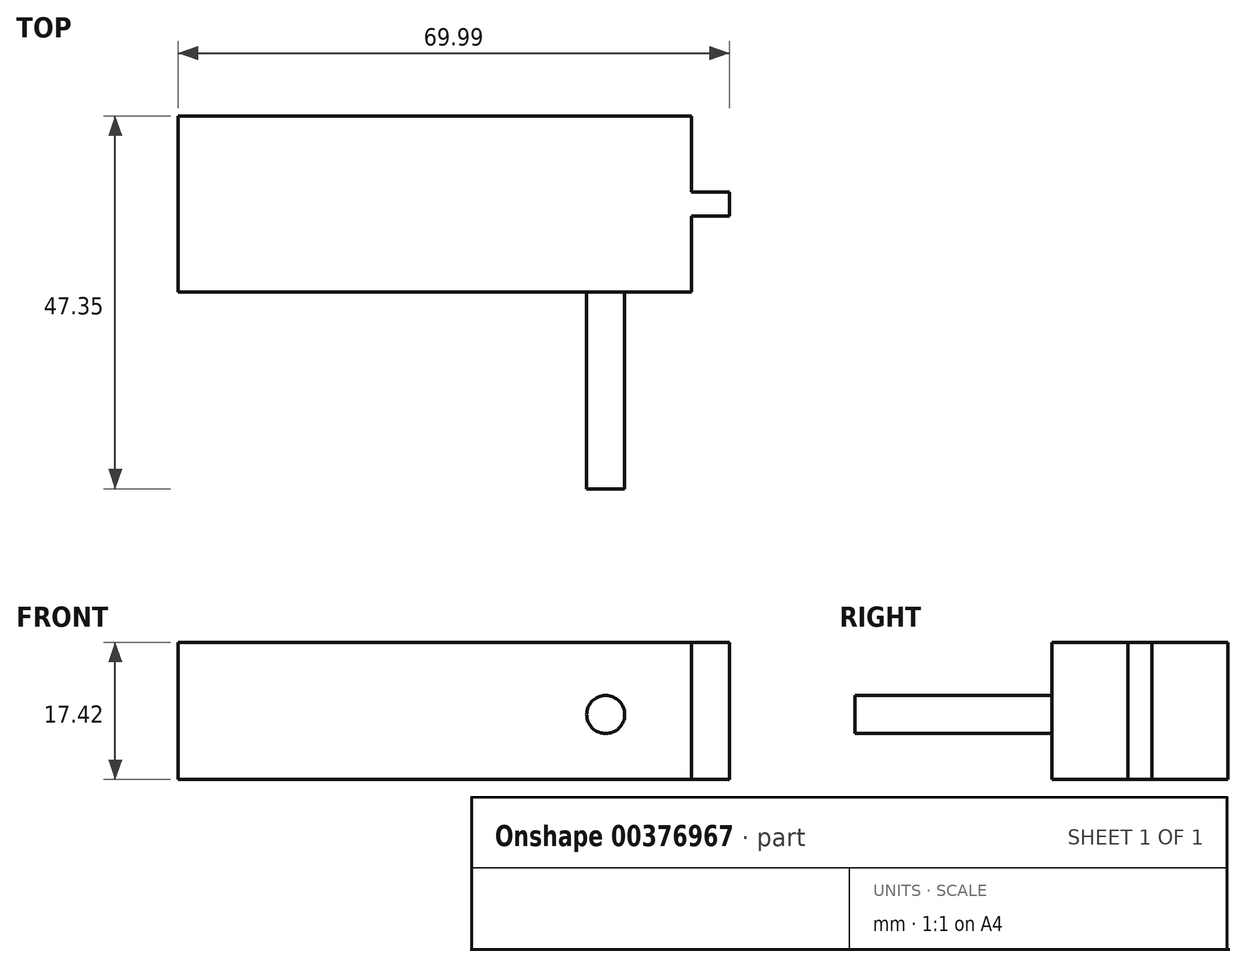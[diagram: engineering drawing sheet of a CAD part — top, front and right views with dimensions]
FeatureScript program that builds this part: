
annotation { "Feature Type Name" : "Feature", "Feature Type Description" : "" }
export const myFeature = defineFeature(function(context is Context, id is Id, definition is map)
    precondition{}
    {
        {
            var Q0;
            Q0=qCreatedBy(makeId("Top.planeOp"),FACE);
            var sketch = newSketch(context, id + "F0", { "sketchPlane" : qUnion([Q0])});
            skLineSegment(sketch, "E0.bottom", {"start": v(-108.7, 5.82) * mm, "end": v(-173.92, 5.82) * mm});
            skLineSegment(sketch, "E0.top", {"start": v(-108.7, 28.17) * mm, "end": v(-173.92, 28.17) * mm});
            skLineSegment(sketch, "E0.left", {"start": v(-108.7, 5.82) * mm, "end": v(-108.7, 28.17) * mm});
            skLineSegment(sketch, "E0.right", {"start": v(-173.92, 5.82) * mm, "end": v(-173.92, 28.17) * mm});
            skPoint(sketch, "E0.middle", {"position": v(-141.31, 17) * mm});
            skLineSegment(sketch, "E1", {"start": v(-119.63, 5.82) * mm, "end": v(-119.63, 3) * mm});
            skLineSegment(sketch, "E2", {"start": v(-119.63, 3) * mm, "end": v(-124.46, 3) * mm});
            skLineSegment(sketch, "E3", {"start": v(-124.46, 3) * mm, "end": v(-124.46, 5.82) * mm});
            skLineSegment(sketch, "E4", {"start": v(-108.7, 17) * mm, "end": v(-103.93, 17) * mm, "construction": true});
            skPoint(sketch, "E4.endSnap0", {"position": v(-108.7, 17) * mm});
            skLineSegment(sketch, "E5", {"start": v(-108.7, 15.5) * mm, "end": v(-103.93, 15.5) * mm});
            skLineSegment(sketch, "E6.MirrorCS", {"start": v(-108.7, 18.5) * mm, "end": v(-103.93, 18.5) * mm});
            skLineSegment(sketch, "E7", {"start": v(-103.93, 15.5) * mm, "end": v(-103.93, 18.5) * mm});
            skSolve(sketch);
        }
        {
            var Q0;
            {var subQ0=sQuery(id+"F0.wireOp",EDGE,"E0.top");Q0=makeQuery(id+"F0.imprint","IMPRINT",FACE,{"disambiguationData":[TD([[makeQuery(id+"F0.imprint","IMPRINT",EDGE,{"derivedFrom":subQ0}),1.0]])]});}
            var Q1;
            {var subQ0=sQuery(id+"F0.wireOp",EDGE,"E5");Q1=makeQuery(id+"F0.imprint","IMPRINT",FACE,{"disambiguationData":[TD([[makeQuery(id+"F0.imprint","IMPRINT",EDGE,{"derivedFrom":subQ0}),1.0]])]});}
            extrude(context, id + "F1", {"entities" : qUnion([Q0, Q1]), "depth" : 17.42 * mm});
        }
        {
            var Q0;
            Q0=makeQuery(id+"F1.opExtrude","SWEPT_FACE",FACE,{"disambiguationData":[OSD([sQuery(id+"F0.wireOp",EDGE,"E0.bottom")])]});
            var sketch = newSketch(context, id + "F2", { "sketchPlane" : qUnion([Q0])});
            skCircle(sketch, "E8", {"center": v(-119.63, 8.25) * mm, "radius": 2.42 * mm});
            skSolve(sketch);
        }
        {
            var Q0;
            Q0=makeQuery(id+"F2.imprint","IMPRINT",FACE,{"disambiguationData":[TD([[makeQuery(id+"F2.imprint","IMPRINT",EDGE,{"derivedFrom":sQuery(id+"F2.wireOp",EDGE,"E8")}),1.0]])]});
            extrude(context, id + "F3", {"entities" : qUnion([Q0]), "operationType" : NewBodyOperationType.ADD, "depth" : 25 * mm});
        }
    });
